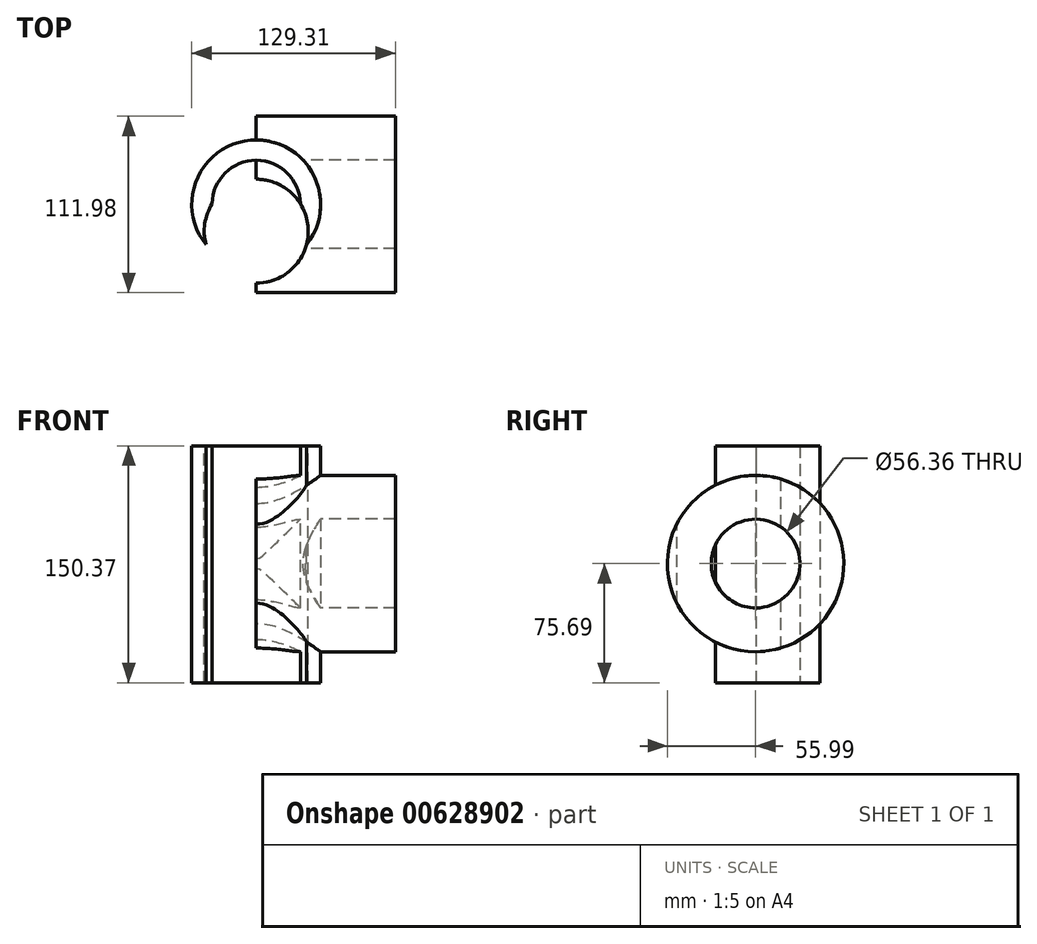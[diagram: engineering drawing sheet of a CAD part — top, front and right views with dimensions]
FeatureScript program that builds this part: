
annotation { "Feature Type Name" : "Feature", "Feature Type Description" : "" }
export const myFeature = defineFeature(function(context is Context, id is Id, definition is map)
    precondition{}
    {
        {
            var Q0;
            Q0=qCreatedBy(makeId("Top.planeOp"),FACE);
            var sketch = newSketch(context, id + "F0", { "sketchPlane" : qUnion([Q0])});
            skCircle(sketch, "E0", {"center": v(0, 0) * mm, "radius": 40.92 * mm});
            skCircle(sketch, "E1", {"center": v(0, 0) * mm, "radius": 28.02 * mm});
            skSolve(sketch);
        }
        {
            var Q0;
            Q0 = qSketchRegion(id + "F0", true);
            extrude(context, id + "F1", {"entities" : qUnion([Q0]), "depth" : 74.68 * mm, "offsetDistance" : 25.4 * mm});
        }
        {
            var Q0;
            Q0 = qSketchRegion(id + "F0", true);
            extrude(context, id + "F2", {"entities" : qUnion([Q0]), "operationType" : NewBodyOperationType.ADD, "oppositeDirection" : true, "depth" : 75.7 * mm, "offsetDistance" : 25.4 * mm});
        }
        {
            var Q0;
            Q0=qCreatedBy(makeId("Right.planeOp"),FACE);
            var sketch = newSketch(context, id + "F3", { "sketchPlane" : qUnion([Q0])});
            skCircle(sketch, "E2", {"center": v(0, 0) * mm, "radius": 56 * mm});
            skCircle(sketch, "E3", {"center": v(0, 0) * mm, "radius": 28.18 * mm});
            skSolve(sketch);
        }
        {
            var Q0;
            Q0 = qSketchRegion(id + "F3", true);
            extrude(context, id + "F4", {"entities" : qUnion([Q0]), "operationType" : NewBodyOperationType.ADD, "depth" : 88.4 * mm, "offsetDistance" : 25.4 * mm});
        }
        {
            var Q0;
            Q0=makeQuery(id+"F1.opExtrude","CAP_FACE",FACE,{"disambiguationData":[OSD([sQuery(id+"F0.wireOp",EDGE,"E0"),sQuery(id+"F0.wireOp",EDGE,"E1")])],"isStart":false});
            var sketch = newSketch(context, id + "F5", { "sketchPlane" : qUnion([Q0])});
            skSolve(sketch);
        }
        {
            var Q0;
            Q0=makeQuery(id+"F5.imprint","IMPRINT",FACE,{"disambiguationData":[TD([[makeQuery(id+"F5.imprint","IMPRINT",EDGE,{"derivedFrom":makeQuery(id+"F1.opExtrude","CAP_EDGE",EDGE,{"disambiguationData":[OSD([sQuery(id+"F0.wireOp",EDGE,"E0")])],"isStart":false})}),1.0]])]});
            var sketch = newSketch(context, id + "F6", { "sketchPlane" : qUnion([Q0])});
            skCircle(sketch, "E4", {"center": v(0, -17.06) * mm, "radius": 33.02 * mm});
            skSolve(sketch);
        }
        {
            var Q0;
            Q0 = qSketchRegion(id + "F6", true);
            extrude(context, id + "F7", {"entities" : qUnion([Q0]), "operationType" : NewBodyOperationType.REMOVE, "oppositeDirection" : true, "depth" : 170.18 * mm, "offsetDistance" : 25.4 * mm});
        }
    });
